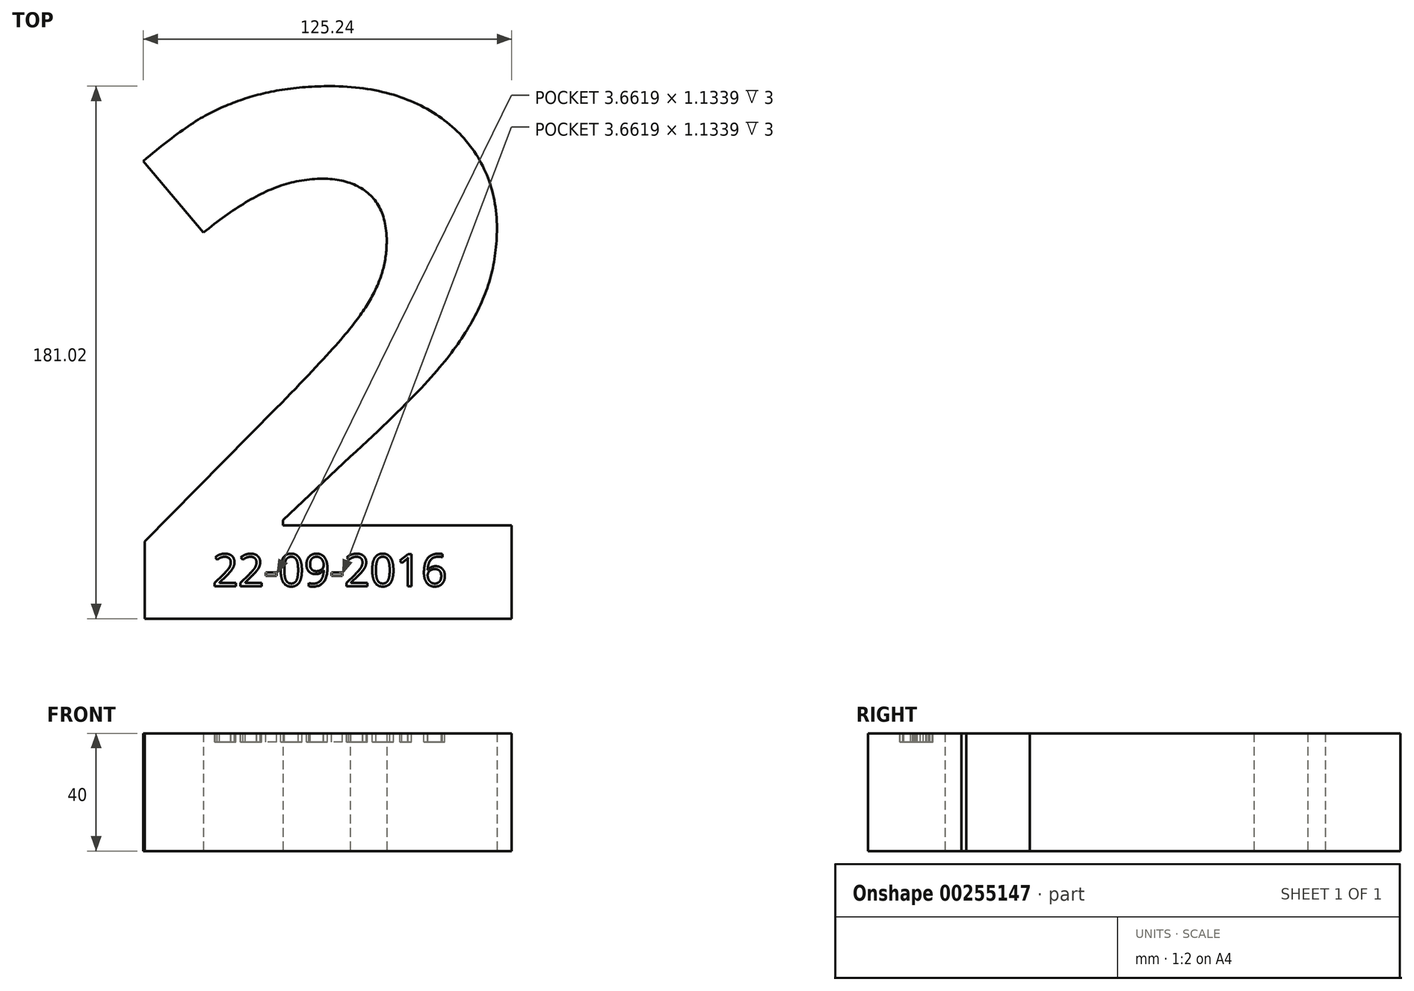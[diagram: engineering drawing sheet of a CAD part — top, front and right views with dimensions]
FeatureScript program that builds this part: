
annotation { "Feature Type Name" : "Feature", "Feature Type Description" : "" }
export const myFeature = defineFeature(function(context is Context, id is Id, definition is map)
    precondition{}
    {
        {
            var Q0;
            Q0=qCreatedBy(makeId("Top.planeOp"),FACE);
            var sketch = newSketch(context, id + "F0", { "sketchPlane" : qUnion([Q0])});
            skText(sketch, "E0", { "text": "2", "fontName": "OpenSans-Bold.ttf"});
            const initialGuessF0  = {"E0": [-0.09938, -0.08592, 1, 0, 0.18]};
            skSetInitialGuess(sketch, initialGuessF0);
            skSolve(sketch);
        }
        {
            var Q0;
            Q0 = qSketchRegion(id + "F0", true);
            extrude(context, id + "F1", {"entities" : qUnion([Q0]), "depth" : 40 * mm});
        }
        {
            var Q0;
            Q0=makeQuery(id+"F1.opExtrude","CAP_FACE",FACE,{"disambiguationData":[OSD([sQuery(id+"F0.wireOp",EDGE,"E0.sketch_text.stroke-0"),sQuery(id+"F0.wireOp",EDGE,"E0.sketch_text.stroke-1"),sQuery(id+"F0.wireOp",EDGE,"E0.sketch_text.stroke-2"),sQuery(id+"F0.wireOp",EDGE,"E0.sketch_text.stroke-3"),sQuery(id+"F0.wireOp",EDGE,"E0.sketch_text.stroke-4"),sQuery(id+"F0.wireOp",EDGE,"E0.sketch_text.stroke-5"),sQuery(id+"F0.wireOp",EDGE,"E0.sketch_text.stroke-6"),sQuery(id+"F0.wireOp",EDGE,"E0.sketch_text.stroke-7"),sQuery(id+"F0.wireOp",EDGE,"E0.sketch_text.stroke-8"),sQuery(id+"F0.wireOp",EDGE,"E0.sketch_text.stroke-9"),sQuery(id+"F0.wireOp",EDGE,"E0.sketch_text.stroke-10"),sQuery(id+"F0.wireOp",EDGE,"E0.sketch_text.stroke-11"),sQuery(id+"F0.wireOp",EDGE,"E0.sketch_text.stroke-12"),sQuery(id+"F0.wireOp",EDGE,"E0.sketch_text.stroke-13"),sQuery(id+"F0.wireOp",EDGE,"E0.sketch_text.stroke-14"),sQuery(id+"F0.wireOp",EDGE,"E0.sketch_text.stroke-15"),sQuery(id+"F0.wireOp",EDGE,"E0.sketch_text.stroke-16"),sQuery(id+"F0.wireOp",EDGE,"E0.sketch_text.stroke-17"),sQuery(id+"F0.wireOp",EDGE,"E0.sketch_text.stroke-18"),sQuery(id+"F0.wireOp",EDGE,"E0.sketch_text.stroke-19"),sQuery(id+"F0.wireOp",EDGE,"E0.sketch_text.stroke-20"),sQuery(id+"F0.wireOp",EDGE,"E0.sketch_text.stroke-21"),sQuery(id+"F0.wireOp",EDGE,"E0.sketch_text.stroke-22"),sQuery(id+"F0.wireOp",EDGE,"E0.sketch_text.stroke-23")])],"isStart":false});
            var sketch = newSketch(context, id + "F2", { "sketchPlane" : qUnion([Q0])});
            skText(sketch, "E1", { "text": "22-09-2016", "fontName": "OpenSans-Regular.ttf"});
            const initialGuessF2  = {"E1": [-0.06626, -0.0749, 1, 0, 0.011]};
            skSetInitialGuess(sketch, initialGuessF2);
            skSolve(sketch);
        }
        {
            var Q0;
            Q0 = qSketchRegion(id + "F2", true);
            extrude(context, id + "F3", {"entities" : qUnion([Q0]), "operationType" : NewBodyOperationType.REMOVE, "oppositeDirection" : true, "depth" : 3 * mm});
        }
    });
